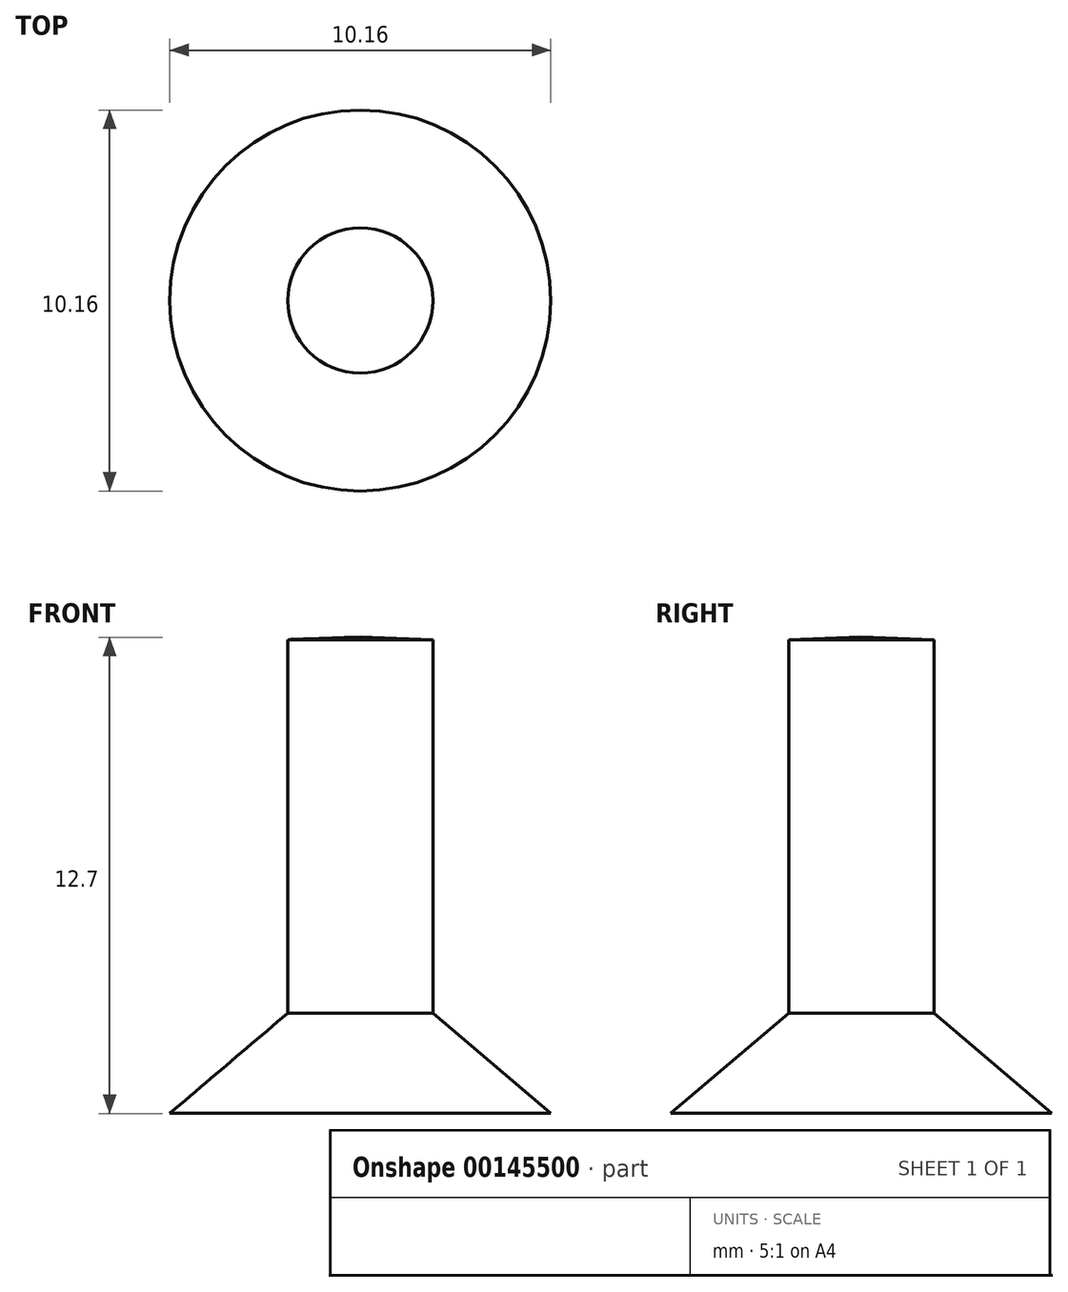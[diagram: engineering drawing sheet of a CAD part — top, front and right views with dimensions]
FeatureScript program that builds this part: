
annotation { "Feature Type Name" : "Feature", "Feature Type Description" : "" }
export const myFeature = defineFeature(function(context is Context, id is Id, definition is map)
    precondition{}
    {
        {
            var Q0;
            Q0=qCreatedBy(makeId("Front.planeOp"),FACE);
            var sketch = newSketch(context, id + "F0", { "sketchPlane" : qUnion([Q0])});
            skLineSegment(sketch, "E0", {"start": v(21.53, 34.97) * mm, "end": v(21.53, 25) * mm});
            skLineSegment(sketch, "E1", {"start": v(21.53, 25) * mm, "end": v(24.67, 22.33) * mm});
            skLineSegment(sketch, "E2", {"start": v(24.67, 22.33) * mm, "end": v(19.6, 22.33) * mm});
            skLineSegment(sketch, "E3", {"start": v(19.6, 22.33) * mm, "end": v(19.6, 35.03) * mm});
            skLineSegment(sketch, "E4", {"start": v(19.6, 35.03) * mm, "end": v(21.53, 34.97) * mm});
            skSolve(sketch);
        }
        {
            var Q0;
            Q0=makeQuery(id+"F0.imprint","IMPRINT",FACE,{"disambiguationData":[TD([[makeQuery(id+"F0.imprint","IMPRINT",EDGE,{"derivedFrom":sQuery(id+"F0.wireOp",EDGE,"E0")}),-1.0]])]});
            var Q1;
            Q1=sQuery(id+"F0.wireOp",EDGE,"E3");
            revolve(context, id + "F1", {"entities" : qUnion([Q0]), "axis" : qUnion([Q1]), "revolveType" : RevolveType.FULL});
        }
    });
